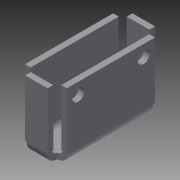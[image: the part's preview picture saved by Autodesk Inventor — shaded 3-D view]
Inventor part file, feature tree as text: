
AUTODESK INVENTOR PART (.ipt)
format: ipt  version: 2013 (Build 170138000, 138)  size: 137,728 bytes
history: native  units: in
note: dims shown in document units (in); Inventor stores cm internally (conversion verified against a paired STEP export)
features: sheet_metal_op x4, sketch x3, other x3
ambient origin geometry x8: Origin, YZ Plane, XZ Plane, XY Plane, X Axis, Y Axis, Z Axis, Center Point
bodies: Solid1 (feature_tree)
feature tree (10):
  sheet_metal_op  "Face1"
  sheet_metal_op  "Flange1"
  sketch  "Sketch1"  dims[d0=2.125in]
  other  "Plate1"
  sketch  "Sketch2"  dims[d1=0.675in]
  other  "Plate2"
  sheet_metal_op  "Bend1"
  sheet_metal_op  "Corner1"
  sketch  "Sketch3"  dims[d2=0.125in d3=0.125in d4=0.0625in d5=0.25in d6=0.125in d7=1.5in d8=90.0deg d9=0.125in d10=0.5in d11=0.125in d12=0.125in d15=0.266in d16=0.266in d17=0.25in d18=0.25in d19=0.25in d20=0.25in d21=0.125in d22=0.0in]
  other  "Cut1"
